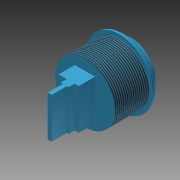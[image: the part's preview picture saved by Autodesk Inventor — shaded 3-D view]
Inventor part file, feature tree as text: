
AUTODESK INVENTOR PART (.ipt)
format: ipt  version: 2013 (Build 170138000, 138)  size: 180,224 bytes
history: native  units: mm
features: extrude x6, sketch x6, fillet x2, thread x1
ambient origin geometry x8: Origin, YZ Plane, XZ Plane, XY Plane, X Axis, Y Axis, Z Axis, Center Point
bodies: Solid1 (feature_tree)
feature tree (15):
  extrude  "Extrusion1"  Depth=33.2mm
  extrude  "Extrusion2"  Depth=29.5mm
  fillet  "Fillet1"  Radius=3.0mm
  fillet  "Fillet2"  Radius=6.4mm
  extrude  "Extrusion5"  Depth=2.95mm
  extrude  "Extrusion7"  Depth=17.0mm TaperAngle=0.0deg
  extrude  "Extrusion8"  Depth=20.0mm
  thread  "Thread1"  [1 undecoded]
  extrude  "Extrusion10"  Depth=4.0mm
  sketch  "Sketch1"  dims[d0=25.0mm d1=33.2mm]
  sketch  "Sketch2"  dims[d2=36.0mm d3=29.5mm d4=3.0mm d5=0.0mm]
  sketch  "Sketch5"  dims[d6=25.0mm d7=33.2mm d8=36.0mm d9=29.5mm d10=6.4mm d11=0.0mm]
  sketch  "Sketch7"  dims[d18=1.5mm d19=2.95mm]
  sketch  "Sketch8"  dims[d23=29.5mm d24=17.0mm d25=0.0mm]
  sketch  "Sketch10"  dims[d30=10.0mm d32=20.0mm d33=8.0mm d34=0.0mm d35=4.0mm d37=20.0mm d38=3.0mm d39=0.0mm d42=10.0mm d43=0.0mm d44=7.5mm d45=0.0mm d46=20.0mm d48=2.0mm]
note: 1 required parameter value undecoded (feature->parameter linkage not recoverable at this tier; creation-order binding heuristic only, values carry confidence <= 0.55)
